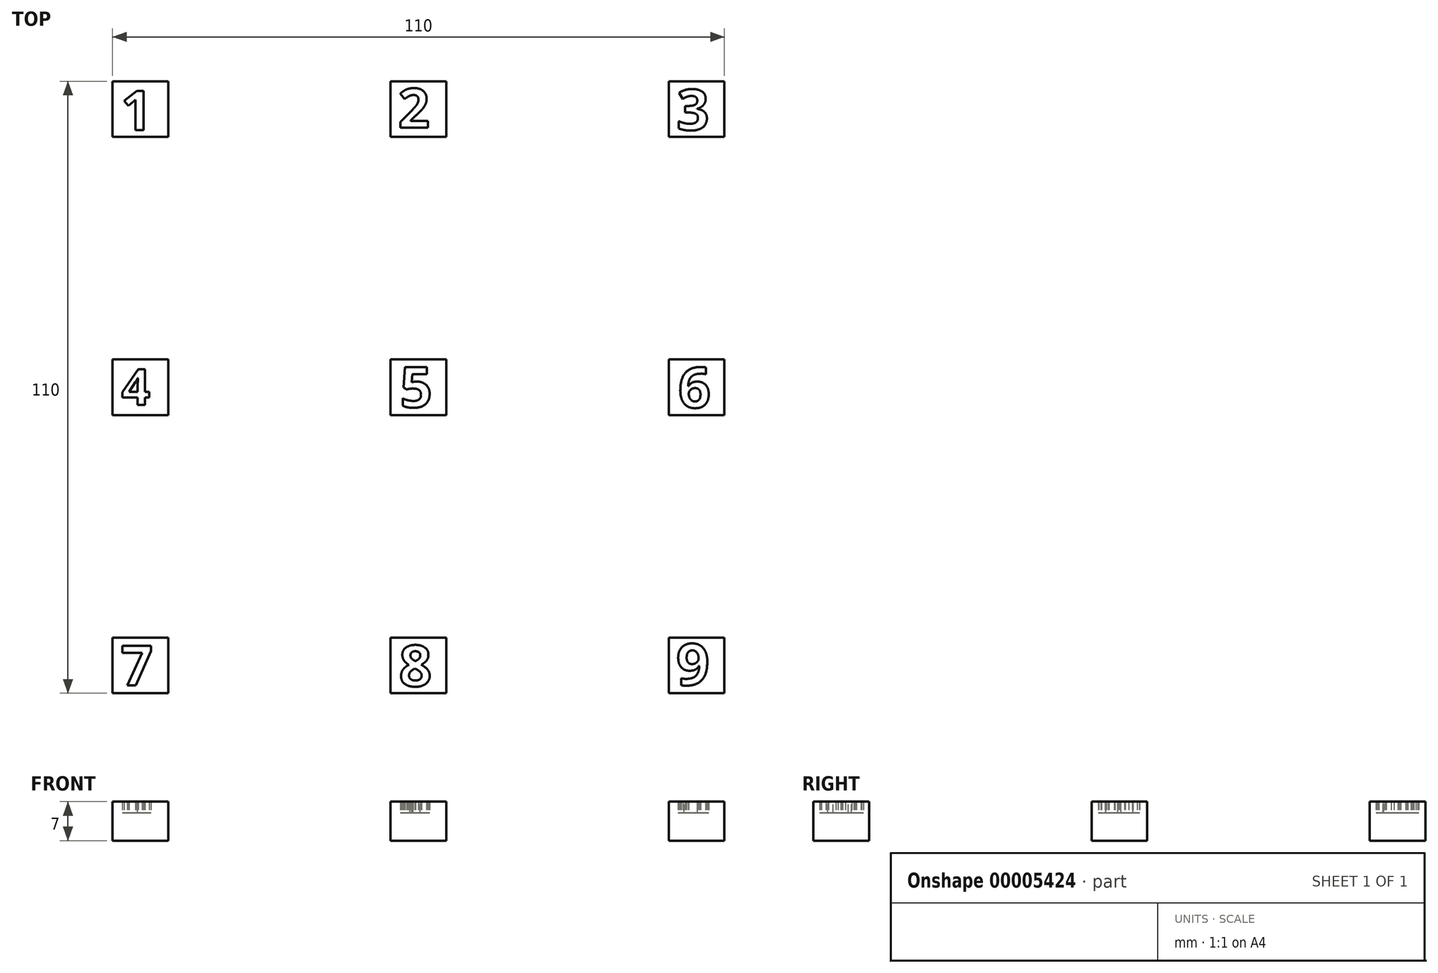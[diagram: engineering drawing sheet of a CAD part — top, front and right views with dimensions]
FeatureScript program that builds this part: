
annotation { "Feature Type Name" : "Feature", "Feature Type Description" : "" }
export const myFeature = defineFeature(function(context is Context, id is Id, definition is map)
    precondition{}
    {
        {
            var Q0;
            Q0=qCreatedBy(makeId("Top.planeOp"),FACE);
            var sketch = newSketch(context, id + "F0", { "sketchPlane" : qUnion([Q0])});
            skLineSegment(sketch, "E0.rect.bottom", {"start": v(50, 50) * mm, "end": v(-50, 50) * mm});
            skLineSegment(sketch, "E0.rect.top", {"start": v(50, -50) * mm, "end": v(-50, -50) * mm});
            skLineSegment(sketch, "E0.rect.left", {"start": v(50, 50) * mm, "end": v(50, -50) * mm});
            skLineSegment(sketch, "E0.rect.right", {"start": v(-50, 50) * mm, "end": v(-50, -50) * mm});
            skPoint(sketch, "E0.rect.middle", {"position": v(0, 0) * mm});
            skLineSegment(sketch, "E1.rect.bottom", {"start": v(-45, 45) * mm, "end": v(-55, 45) * mm});
            skLineSegment(sketch, "E1.rect.top", {"start": v(-45, 55) * mm, "end": v(-55, 55) * mm});
            skLineSegment(sketch, "E1.rect.left", {"start": v(-45, 45) * mm, "end": v(-45, 55) * mm});
            skLineSegment(sketch, "E1.rect.right", {"start": v(-55, 45) * mm, "end": v(-55, 55) * mm});
            skPoint(sketch, "E1.rect.middle", {"position": v(-50, 50) * mm});
            skPoint(sketch, "E2.0.1.4", {"position": v(-50, 0) * mm});
            skLineSegment(sketch, "E2.0.1.5", {"start": v(-45, 5) * mm, "end": v(-55, 5) * mm});
            skLineSegment(sketch, "E2.0.1.6", {"start": v(-45, -5) * mm, "end": v(-55, -5) * mm});
            skLineSegment(sketch, "E2.0.1.7", {"start": v(-55, -5) * mm, "end": v(-55, 5) * mm});
            skLineSegment(sketch, "E2.0.1.8", {"start": v(-45, -5) * mm, "end": v(-45, 5) * mm});
            skPoint(sketch, "E2.0.2.4", {"position": v(-50, -50) * mm});
            skLineSegment(sketch, "E2.0.2.5", {"start": v(-45, -45) * mm, "end": v(-55, -45) * mm});
            skLineSegment(sketch, "E2.0.2.6", {"start": v(-45, -55) * mm, "end": v(-55, -55) * mm});
            skLineSegment(sketch, "E2.0.2.7", {"start": v(-55, -55) * mm, "end": v(-55, -45) * mm});
            skLineSegment(sketch, "E2.0.2.8", {"start": v(-45, -55) * mm, "end": v(-45, -45) * mm});
            skPoint(sketch, "E2.1.0.4", {"position": v(0, 50) * mm});
            skLineSegment(sketch, "E2.1.0.5", {"start": v(5, 55) * mm, "end": v(-5, 55) * mm});
            skLineSegment(sketch, "E2.1.0.6", {"start": v(5, 45) * mm, "end": v(-5, 45) * mm});
            skLineSegment(sketch, "E2.1.0.7", {"start": v(-5, 45) * mm, "end": v(-5, 55) * mm});
            skLineSegment(sketch, "E2.1.0.8", {"start": v(5, 45) * mm, "end": v(5, 55) * mm});
            skLineSegment(sketch, "E2.1.1.5", {"start": v(5, 5) * mm, "end": v(-5, 5) * mm});
            skLineSegment(sketch, "E2.1.1.6", {"start": v(5, -5) * mm, "end": v(-5, -5) * mm});
            skLineSegment(sketch, "E2.1.1.7", {"start": v(-5, -5) * mm, "end": v(-5, 5) * mm});
            skLineSegment(sketch, "E2.1.1.8", {"start": v(5, -5) * mm, "end": v(5, 5) * mm});
            skPoint(sketch, "E2.1.2.4", {"position": v(0, -50) * mm});
            skLineSegment(sketch, "E2.1.2.5", {"start": v(5, -45) * mm, "end": v(-5, -45) * mm});
            skLineSegment(sketch, "E2.1.2.6", {"start": v(5, -55) * mm, "end": v(-5, -55) * mm});
            skLineSegment(sketch, "E2.1.2.7", {"start": v(-5, -55) * mm, "end": v(-5, -45) * mm});
            skLineSegment(sketch, "E2.1.2.8", {"start": v(5, -55) * mm, "end": v(5, -45) * mm});
            skPoint(sketch, "E2.2.0.4", {"position": v(50, 50) * mm});
            skLineSegment(sketch, "E2.2.0.5", {"start": v(55, 55) * mm, "end": v(45, 55) * mm});
            skLineSegment(sketch, "E2.2.0.6", {"start": v(55, 45) * mm, "end": v(45, 45) * mm});
            skLineSegment(sketch, "E2.2.0.7", {"start": v(45, 45) * mm, "end": v(45, 55) * mm});
            skLineSegment(sketch, "E2.2.0.8", {"start": v(55, 45) * mm, "end": v(55, 55) * mm});
            skPoint(sketch, "E2.2.1.4", {"position": v(50, 0) * mm});
            skLineSegment(sketch, "E2.2.1.5", {"start": v(55, 5) * mm, "end": v(45, 5) * mm});
            skLineSegment(sketch, "E2.2.1.6", {"start": v(55, -5) * mm, "end": v(45, -5) * mm});
            skLineSegment(sketch, "E2.2.1.7", {"start": v(45, -5) * mm, "end": v(45, 5) * mm});
            skLineSegment(sketch, "E2.2.1.8", {"start": v(55, -5) * mm, "end": v(55, 5) * mm});
            skPoint(sketch, "E2.2.2.4", {"position": v(50, -50) * mm});
            skLineSegment(sketch, "E2.2.2.5", {"start": v(55, -45) * mm, "end": v(45, -45) * mm});
            skLineSegment(sketch, "E2.2.2.6", {"start": v(55, -55) * mm, "end": v(45, -55) * mm});
            skLineSegment(sketch, "E2.2.2.7", {"start": v(45, -55) * mm, "end": v(45, -45) * mm});
            skLineSegment(sketch, "E2.2.2.8", {"start": v(55, -55) * mm, "end": v(55, -45) * mm});
            skLineSegment(sketch, "E2.direction1", {"start": v(-55, 55) * mm, "end": v(-5, 55) * mm, "construction": true});
            skLineSegment(sketch, "E2.direction2", {"start": v(-55, 55) * mm, "end": v(-55, 5) * mm, "construction": true});
            skSolve(sketch);
        }
        {
            var Q0;
            {var subQ0=sQuery(id+"F0.wireOp",EDGE,"E2.2.1.7");Q0=makeQuery(id+"F0.imprint","IMPRINT",FACE,{"disambiguationData":[TD([[makeQuery(id+"F0.imprint","IMPRINT",EDGE,{"derivedFrom":subQ0}),-1.0]])]});}
            var Q1;
            {var subQ3=sQuery(id+"F0.wireOp",EDGE,"E2.1.2.5");Q1=makeQuery(id+"F0.imprint","IMPRINT",FACE,{"disambiguationData":[TD([[makeQuery(id+"F0.imprint","IMPRINT",EDGE,{"derivedFrom":subQ3}),1.0]])]});}
            var Q2;
            {var subQ3=sQuery(id+"F0.wireOp",EDGE,"E2.0.1.8");Q2=makeQuery(id+"F0.imprint","IMPRINT",FACE,{"disambiguationData":[TD([[makeQuery(id+"F0.imprint","IMPRINT",EDGE,{"derivedFrom":subQ3}),1.0]])]});}
            var Q3;
            {var subQ1=sQuery(id+"F0.wireOp",EDGE,"E0.rect.top");var subQ5=sQuery(id+"F0.wireOp",EDGE,"E0.rect.right");var subQ7=makeQuery(id+"F0.imprint","INTERSECT",VERTEX,{"derivedFrom":[subQ1,subQ5]});Q3=makeQuery(id+"F0.imprint","IMPRINT",FACE,{"disambiguationData":[TD([[makeQuery(id+"F0.imprint","IMPRINT",EDGE,{"disambiguationData":[TD([[subQ7,1.0]])],"derivedFrom":subQ1}),-1.0]])]});}
            var Q4;
            {var subQ3=sQuery(id+"F0.wireOp",EDGE,"E2.2.0.5");Q4=makeQuery(id+"F0.imprint","IMPRINT",FACE,{"disambiguationData":[TD([[makeQuery(id+"F0.imprint","IMPRINT",EDGE,{"derivedFrom":subQ3}),1.0]])]});}
            var Q5;
            {var subQ3=sQuery(id+"F0.wireOp",EDGE,"E2.1.0.5");Q5=makeQuery(id+"F0.imprint","IMPRINT",FACE,{"disambiguationData":[TD([[makeQuery(id+"F0.imprint","IMPRINT",EDGE,{"derivedFrom":subQ3}),1.0]])]});}
            var Q6;
            {var subQ4=sQuery(id+"F0.wireOp",EDGE,"E1.rect.top");Q6=makeQuery(id+"F0.imprint","IMPRINT",FACE,{"disambiguationData":[TD([[makeQuery(id+"F0.imprint","IMPRINT",EDGE,{"derivedFrom":subQ4}),1.0]])]});}
            var Q7;
            {var subQ4=sQuery(id+"F0.wireOp",EDGE,"E2.2.2.6");Q7=makeQuery(id+"F0.imprint","IMPRINT",FACE,{"disambiguationData":[TD([[makeQuery(id+"F0.imprint","IMPRINT",EDGE,{"derivedFrom":subQ4}),-1.0]])]});}
            var Q8;
            {var subQ3=sQuery(id+"F0.wireOp",EDGE,"E2.1.2.6");Q8=makeQuery(id+"F0.imprint","IMPRINT",FACE,{"disambiguationData":[TD([[makeQuery(id+"F0.imprint","IMPRINT",EDGE,{"derivedFrom":subQ3}),-1.0]])]});}
            var Q9;
            {var subQ3=sQuery(id+"F0.wireOp",EDGE,"E2.0.2.6");Q9=makeQuery(id+"F0.imprint","IMPRINT",FACE,{"disambiguationData":[TD([[makeQuery(id+"F0.imprint","IMPRINT",EDGE,{"derivedFrom":subQ3}),-1.0]])]});}
            var Q10;
            {var subQ0=sQuery(id+"F0.wireOp",EDGE,"E2.2.1.8");Q10=makeQuery(id+"F0.imprint","IMPRINT",FACE,{"disambiguationData":[TD([[makeQuery(id+"F0.imprint","IMPRINT",EDGE,{"derivedFrom":subQ0}),1.0]])]});}
            var Q11;
            {var subQ0=sQuery(id+"F0.wireOp",EDGE,"E2.0.1.7");Q11=makeQuery(id+"F0.imprint","IMPRINT",FACE,{"disambiguationData":[TD([[makeQuery(id+"F0.imprint","IMPRINT",EDGE,{"derivedFrom":subQ0}),-1.0]])]});}
            var Q12;
            Q12=makeQuery(id+"F0.imprint","IMPRINT",FACE,{"disambiguationData":[TD([[makeQuery(id+"F0.imprint","IMPRINT",EDGE,{"derivedFrom":sQuery(id+"F0.wireOp",EDGE,"E2.1.1.5")}),1.0]])]});
            var Q13;
            {var subQ1=sQuery(id+"F0.wireOp",EDGE,"E0.rect.bottom");var subQ5=sQuery(id+"F0.wireOp",EDGE,"E0.rect.left");var subQ7=makeQuery(id+"F0.imprint","INTERSECT",VERTEX,{"derivedFrom":[subQ1,subQ5]});Q13=makeQuery(id+"F0.imprint","IMPRINT",FACE,{"disambiguationData":[TD([[makeQuery(id+"F0.imprint","IMPRINT",EDGE,{"disambiguationData":[TD([[subQ7,-1.0]])],"derivedFrom":subQ1}),1.0]])]});}
            var Q14;
            {var subQ3=sQuery(id+"F0.wireOp",EDGE,"E2.1.0.6");Q14=makeQuery(id+"F0.imprint","IMPRINT",FACE,{"disambiguationData":[TD([[makeQuery(id+"F0.imprint","IMPRINT",EDGE,{"derivedFrom":subQ3}),-1.0]])]});}
            var Q15;
            {var subQ1=sQuery(id+"F0.wireOp",EDGE,"E0.rect.bottom");var subQ5=sQuery(id+"F0.wireOp",EDGE,"E0.rect.right");var subQ7=makeQuery(id+"F0.imprint","INTERSECT",VERTEX,{"derivedFrom":[subQ1,subQ5]});Q15=makeQuery(id+"F0.imprint","IMPRINT",FACE,{"disambiguationData":[TD([[makeQuery(id+"F0.imprint","IMPRINT",EDGE,{"disambiguationData":[TD([[subQ7,1.0]])],"derivedFrom":subQ1}),1.0]])]});}
            var Q16;
            {var subQ1=sQuery(id+"F0.wireOp",EDGE,"E0.rect.top");var subQ5=sQuery(id+"F0.wireOp",EDGE,"E0.rect.left");var subQ7=makeQuery(id+"F0.imprint","INTERSECT",VERTEX,{"derivedFrom":[subQ1,subQ5]});Q16=makeQuery(id+"F0.imprint","IMPRINT",FACE,{"disambiguationData":[TD([[makeQuery(id+"F0.imprint","IMPRINT",EDGE,{"disambiguationData":[TD([[subQ7,-1.0]])],"derivedFrom":subQ1}),-1.0]])]});}
            extrude(context, id + "F1", {"entities" : qUnion([Q0, Q1, Q2, Q3, Q4, Q5, Q6, Q7, Q8, Q9, Q10, Q11, Q12, Q13, Q14, Q15, Q16]), "depth" : 5 * mm});
        }
        {
            var Q0;
            Q0=makeQuery(id+"F1.opExtrude","CAP_FACE",FACE,{"disambiguationData":[OSD([sQuery(id+"F0.wireOp",EDGE,"E1.rect.bottom"),sQuery(id+"F0.wireOp",EDGE,"E1.rect.top"),sQuery(id+"F0.wireOp",EDGE,"E1.rect.left"),sQuery(id+"F0.wireOp",EDGE,"E1.rect.right")])],"isStart":false});
            var sketch = newSketch(context, id + "F2", { "sketchPlane" : qUnion([Q0])});
            skLineSegment(sketch, "E3.0.0", {"start": v(-55, 45) * mm, "end": v(-45, 45) * mm});
            skLineSegment(sketch, "E3.0.1", {"start": v(-45, 45) * mm, "end": v(-45, 55) * mm});
            skLineSegment(sketch, "E3.0.2", {"start": v(-45, 55) * mm, "end": v(-55, 55) * mm});
            skLineSegment(sketch, "E3.0.3", {"start": v(-55, 55) * mm, "end": v(-55, 45) * mm});
            skLineSegment(sketch, "E4.0.0", {"start": v(-5, 55) * mm, "end": v(-5, 45) * mm});
            skLineSegment(sketch, "E4.0.1", {"start": v(-5, 45) * mm, "end": v(5, 45) * mm});
            skLineSegment(sketch, "E4.0.2", {"start": v(5, 45) * mm, "end": v(5, 55) * mm});
            skLineSegment(sketch, "E4.0.3", {"start": v(5, 55) * mm, "end": v(-5, 55) * mm});
            skLineSegment(sketch, "E5.0.0", {"start": v(45, 55) * mm, "end": v(45, 45) * mm});
            skLineSegment(sketch, "E5.0.1", {"start": v(45, 45) * mm, "end": v(55, 45) * mm});
            skLineSegment(sketch, "E5.0.2", {"start": v(55, 45) * mm, "end": v(55, 55) * mm});
            skLineSegment(sketch, "E5.0.3", {"start": v(55, 55) * mm, "end": v(45, 55) * mm});
            skLineSegment(sketch, "E6.0.0", {"start": v(45, -5) * mm, "end": v(55, -5) * mm});
            skLineSegment(sketch, "E6.0.1", {"start": v(55, -5) * mm, "end": v(55, 5) * mm});
            skLineSegment(sketch, "E6.0.2", {"start": v(55, 5) * mm, "end": v(45, 5) * mm});
            skLineSegment(sketch, "E6.0.3", {"start": v(45, 5) * mm, "end": v(45, -5) * mm});
            skLineSegment(sketch, "E7.0.0", {"start": v(5, -5) * mm, "end": v(5, 5) * mm});
            skLineSegment(sketch, "E7.0.1", {"start": v(5, 5) * mm, "end": v(-5, 5) * mm});
            skLineSegment(sketch, "E7.0.2", {"start": v(-5, 5) * mm, "end": v(-5, -5) * mm});
            skLineSegment(sketch, "E7.0.3", {"start": v(-5, -5) * mm, "end": v(5, -5) * mm});
            skLineSegment(sketch, "E8.0.0", {"start": v(-45, 5) * mm, "end": v(-55, 5) * mm});
            skLineSegment(sketch, "E8.0.1", {"start": v(-55, 5) * mm, "end": v(-55, -5) * mm});
            skLineSegment(sketch, "E8.0.2", {"start": v(-55, -5) * mm, "end": v(-45, -5) * mm});
            skLineSegment(sketch, "E8.0.3", {"start": v(-45, -5) * mm, "end": v(-45, 5) * mm});
            skLineSegment(sketch, "E9.0.0", {"start": v(-55, -55) * mm, "end": v(-45, -55) * mm});
            skLineSegment(sketch, "E9.0.1", {"start": v(-45, -55) * mm, "end": v(-45, -45) * mm});
            skLineSegment(sketch, "E9.0.2", {"start": v(-45, -45) * mm, "end": v(-55, -45) * mm});
            skLineSegment(sketch, "E9.0.3", {"start": v(-55, -45) * mm, "end": v(-55, -55) * mm});
            skLineSegment(sketch, "E10.0.0", {"start": v(-5, -55) * mm, "end": v(5, -55) * mm});
            skLineSegment(sketch, "E10.0.1", {"start": v(5, -55) * mm, "end": v(5, -45) * mm});
            skLineSegment(sketch, "E10.0.2", {"start": v(5, -45) * mm, "end": v(-5, -45) * mm});
            skLineSegment(sketch, "E10.0.3", {"start": v(-5, -45) * mm, "end": v(-5, -55) * mm});
            skLineSegment(sketch, "E11.0.0", {"start": v(55, -45) * mm, "end": v(45, -45) * mm});
            skLineSegment(sketch, "E11.0.1", {"start": v(45, -45) * mm, "end": v(45, -55) * mm});
            skLineSegment(sketch, "E11.0.2", {"start": v(45, -55) * mm, "end": v(55, -55) * mm});
            skLineSegment(sketch, "E11.0.3", {"start": v(55, -55) * mm, "end": v(55, -45) * mm});
            skText(sketch, "E12", { "text": "1", "fontName": "OpenSans-Bold.ttf"});
            skText(sketch, "E13", { "text": "2", "fontName": "OpenSans-Bold.ttf"});
            skText(sketch, "E14", { "text": "3", "fontName": "OpenSans-Bold.ttf"});
            skText(sketch, "E15", { "text": "4", "fontName": "OpenSans-Bold.ttf"});
            skText(sketch, "E16", { "text": "5", "fontName": "OpenSans-Bold.ttf"});
            skText(sketch, "E17", { "text": "6", "fontName": "OpenSans-Bold.ttf"});
            skText(sketch, "E18", { "text": "7", "fontName": "OpenSans-Bold.ttf"});
            skText(sketch, "E19", { "text": "8", "fontName": "OpenSans-Bold.ttf"});
            skText(sketch, "E20", { "text": "9", "fontName": "OpenSans-Bold.ttf"});
            const initialGuessF2  = {"E12": [-0.05348, 0.04625, 1, 0, 0.0071], "E13": [-0.00365, 0.04666, 1, 0, 0.0071], "E14": [0.04642, 0.04625, 1, 0, 0.00734], "E15": [-0.05337, -0.00318, 1, 0, 0.00647], "E16": [-0.00333, -0.0036, 1, 0, 0.0073], "E17": [0.04671, -0.00367, 1, 0, 0.0073], "E18": [-0.05348, -0.0536, 1, 0, 0.0072], "E19": [-0.0035, -0.05375, 1, 0, 0.00741], "E20": [0.04635, -0.05354, 1, 0, 0.00748]};
            skSetInitialGuess(sketch, initialGuessF2);
            skSolve(sketch);
        }
        {
            var Q0;
            Q0 = qSketchRegion(id + "F2", true);
            var Q1;
            Q1=makeQuery(id+"F2.imprint","IMPRINT",FACE,{"disambiguationData":[TD([[makeQuery(id+"F2.imprint","IMPRINT",EDGE,{"derivedFrom":sQuery(id+"F2.wireOp",EDGE,"E17.sketch_text.stroke-17")}),1.0]])]});
            var Q2;
            Q2=makeQuery(id+"F2.imprint","IMPRINT",FACE,{"disambiguationData":[TD([[makeQuery(id+"F2.imprint","IMPRINT",EDGE,{"derivedFrom":sQuery(id+"F2.wireOp",EDGE,"E19.sketch_text.stroke-16")}),1.0]])]});
            var Q3;
            Q3=makeQuery(id+"F2.imprint","IMPRINT",FACE,{"disambiguationData":[TD([[makeQuery(id+"F2.imprint","IMPRINT",EDGE,{"derivedFrom":sQuery(id+"F2.wireOp",EDGE,"E19.sketch_text.stroke-23")}),1.0]])]});
            var Q4;
            Q4=makeQuery(id+"F2.imprint","IMPRINT",FACE,{"disambiguationData":[TD([[makeQuery(id+"F2.imprint","IMPRINT",EDGE,{"derivedFrom":sQuery(id+"F2.wireOp",EDGE,"E20.sketch_text.stroke-18")}),1.0]])]});
            var Q5;
            Q5=makeQuery(id+"F2.imprint","IMPRINT",FACE,{"disambiguationData":[TD([[makeQuery(id+"F2.imprint","IMPRINT",EDGE,{"derivedFrom":sQuery(id+"F2.wireOp",EDGE,"E15.sketch_text.stroke-11")}),1.0]])]});
            extrude(context, id + "F3", {"entities" : qUnion([Q0, Q1, Q2, Q3, Q4, Q5]), "operationType" : NewBodyOperationType.ADD, "depth" : 2 * mm});
        }
    });
